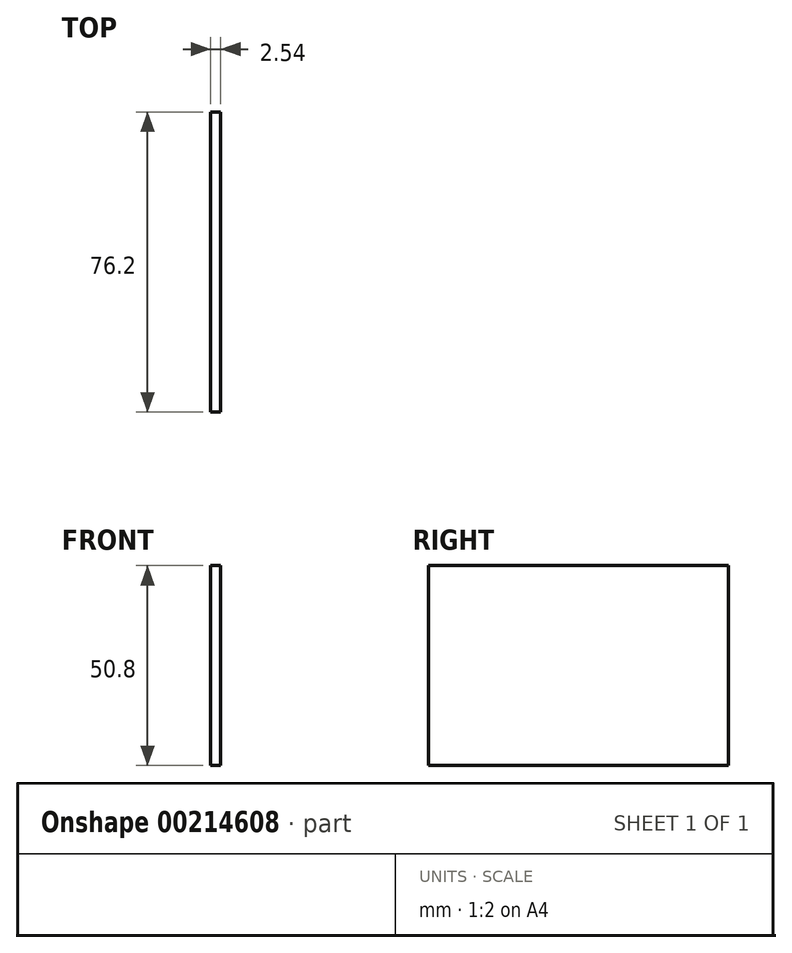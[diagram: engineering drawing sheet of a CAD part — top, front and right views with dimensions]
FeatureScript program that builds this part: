
annotation { "Feature Type Name" : "Feature", "Feature Type Description" : "" }
export const myFeature = defineFeature(function(context is Context, id is Id, definition is map)
    precondition{}
    {
        {
            var Q0;
            Q0=qCreatedBy(makeId("Right.planeOp"),FACE);
            var sketch = newSketch(context, id + "F0", { "sketchPlane" : qUnion([Q0])});
            skLineSegment(sketch, "E0.bottom", {"start": v(-27.22, 26.08) * mm, "end": v(48.98, 26.08) * mm});
            skLineSegment(sketch, "E0.top", {"start": v(-27.22, -24.72) * mm, "end": v(48.98, -24.72) * mm});
            skLineSegment(sketch, "E0.left", {"start": v(-27.22, 26.08) * mm, "end": v(-27.22, -24.72) * mm});
            skLineSegment(sketch, "E0.right", {"start": v(48.98, 26.08) * mm, "end": v(48.98, -24.72) * mm});
            skSolve(sketch);
        }
        {
            var Q0;
            Q0=makeQuery(id+"F0.imprint","IMPRINT",FACE,{"disambiguationData":[TD([[makeQuery(id+"F0.imprint","IMPRINT",EDGE,{"derivedFrom":sQuery(id+"F0.wireOp",EDGE,"E0.bottom")}),-1.0]])]});
            extrude(context, id + "F1", {"entities" : qUnion([Q0]), "depth" : 2.54 * mm});
        }
    });
